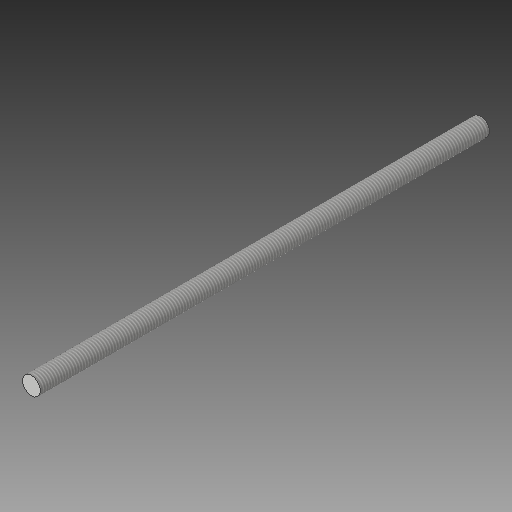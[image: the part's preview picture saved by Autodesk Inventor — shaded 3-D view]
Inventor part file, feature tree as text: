
AUTODESK INVENTOR PART (.ipt)
format: ipt  version: 2017 SP1 (Build 210196100, 196)  size: 95,232 bytes
history: native  units: mm
features: extrude x1, thread x1, sketch x1
ambient origin geometry x8: Origin, YZ Plane, XZ Plane, XY Plane, X Axis, Y Axis, Z Axis, Center Point
bodies: Solid1 (feature_tree)
feature tree (3):
  extrude  "Extrusion1"  Depth=200.0mm TaperAngle=0.0deg
  thread  "Thread1"  [1 undecoded]
  sketch  "Sketch1"  dims[d0=8.0mm d1=200.0mm d2=0.0mm d3=10.0mm d4=0.0mm]
note: 1 required parameter value undecoded (feature->parameter linkage not recoverable at this tier; creation-order binding heuristic only, values carry confidence <= 0.55)
